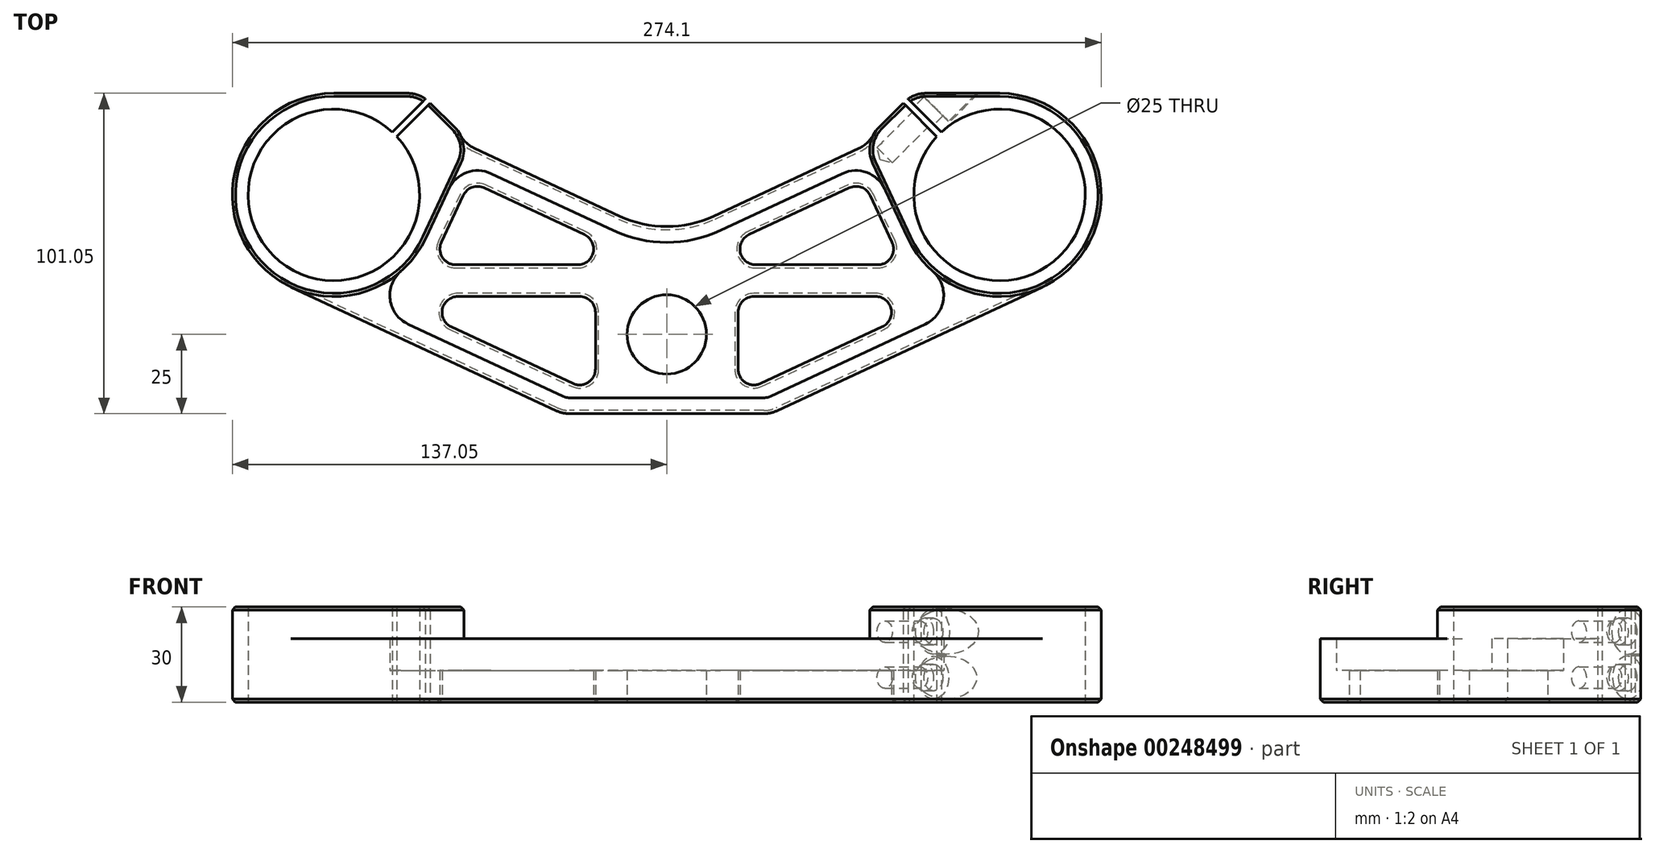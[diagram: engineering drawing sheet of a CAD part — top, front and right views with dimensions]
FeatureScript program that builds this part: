
annotation { "Feature Type Name" : "Feature", "Feature Type Description" : "" }
export const myFeature = defineFeature(function(context is Context, id is Id, definition is map)
    precondition{}
    {
        {
            var Q0;
            Q0=qCreatedBy(makeId("Top.planeOp"),FACE);
            var sketch = newSketch(context, id + "F0", { "sketchPlane" : qUnion([Q0])});
            skCircle(sketch, "E0", {"center": v(0, 0) * mm, "radius": 12.5 * mm});
            skArc(sketch, "E1", {"start": v(-86.6, 63.82) * mm, "mid": v(-124.13, 24.87) * mm, "end": v(-85.18, 62.4) * mm});
            skArc(sketch, "E2", {"start": v(85.18, 62.4) * mm, "mid": v(124.13, 24.87) * mm, "end": v(86.6, 63.82) * mm});
            skArc(sketch, "E3", {"start": v(75.95, 30.46) * mm, "mid": v(132.03, 26.78) * mm, "end": v(105, 76.05) * mm});
            skLineSegment(sketch, "E4", {"start": v(-30.65, -25) * mm, "end": v(30.65, -25) * mm});
            skLineSegment(sketch, "E5", {"start": v(-118.9, 15.12) * mm, "end": v(-34.88, -24.06) * mm});
            skLineSegment(sketch, "E6", {"start": v(118.54, 14.95) * mm, "end": v(34.88, -24.06) * mm});
            skLineSegment(sketch, "E7", {"start": v(-105, 76.05) * mm, "end": v(-81.8, 76.05) * mm});
            skLineSegment(sketch, "E8", {"start": v(-74.6, 73) * mm, "end": v(-66.94, 65.34) * mm});
            skLineSegment(sketch, "E9", {"start": v(74.6, 73) * mm, "end": v(66.94, 65.34) * mm});
            skLineSegment(sketch, "E10.trimOffspring", {"start": v(81.8, 76.05) * mm, "end": v(105, 76.05) * mm});
            skArc(sketch, "E11.filletArc", {"start": v(-76.13, 74.29) * mm, "mid": v(-78.83, 75.6) * mm, "end": v(-81.8, 76.05) * mm});
            skArc(sketch, "E12.filletArc", {"start": v(81.8, 76.05) * mm, "mid": v(78.83, 75.6) * mm, "end": v(76.13, 74.29) * mm});
            skPoint(sketch, "E13.visualSharp", {"position": v(-32.87, -25) * mm});
            skArc(sketch, "E13.filletArc", {"start": v(-34.88, -24.06) * mm, "mid": v(-32.81, -24.76) * mm, "end": v(-30.65, -25) * mm});
            skPoint(sketch, "E14.visualSharp", {"position": v(32.87, -25) * mm});
            skArc(sketch, "E14.filletArc", {"start": v(30.65, -25) * mm, "mid": v(32.81, -24.76) * mm, "end": v(34.88, -24.06) * mm});
            skLineSegment(sketch, "E15", {"start": v(-75.95, 30.46) * mm, "end": v(-64.95, 54.04) * mm});
            skLineSegment(sketch, "E16", {"start": v(75.95, 30.46) * mm, "end": v(64.95, 54.04) * mm});
            skArc(sketch, "E17", {"start": v(-65.2, 63) * mm, "mid": v(-65.99, 64.24) * mm, "end": v(-66.94, 65.34) * mm});
            skArc(sketch, "E18", {"start": v(66.94, 65.34) * mm, "mid": v(65.99, 64.24) * mm, "end": v(65.2, 63) * mm});
            skLineSegment(sketch, "E19", {"start": v(-85.18, 62.4) * mm, "end": v(-74.6, 73) * mm});
            skLineSegment(sketch, "E20", {"start": v(-86.6, 63.82) * mm, "end": v(-76.13, 74.29) * mm});
            skLineSegment(sketch, "E21", {"start": v(85.18, 62.4) * mm, "end": v(74.6, 73) * mm});
            skLineSegment(sketch, "E22", {"start": v(86.6, 63.82) * mm, "end": v(76.13, 74.29) * mm});
            skLineSegment(sketch, "E23", {"start": v(-68, 2.42) * mm, "end": v(-29.61, -15.48) * mm});
            skLineSegment(sketch, "E24", {"start": v(68, 2.42) * mm, "end": v(29.61, -15.48) * mm});
            skLineSegment(sketch, "E25", {"start": v(-65.89, 11.95) * mm, "end": v(-27.5, 11.95) * mm});
            skPoint(sketch, "E26.visualSharp", {"position": v(0, 31.47) * mm});
            skLineSegment(sketch, "E27", {"start": v(-66.55, 21.95) * mm, "end": v(-28.1, 21.95) * mm});
            skLineSegment(sketch, "E28", {"start": v(-55.46, 50.74) * mm, "end": v(-16.9, 32.77) * mm});
            skLineSegment(sketch, "E29", {"start": v(55.46, 50.74) * mm, "end": v(16.9, 32.77) * mm});
            skArc(sketch, "E30.filletArc", {"start": v(-16.9, 32.77) * mm, "mid": v(0, 29.02) * mm, "end": v(16.9, 32.77) * mm});
            skLineSegment(sketch, "E31", {"start": v(-57.57, 46.21) * mm, "end": v(-25.98, 31.48) * mm});
            skLineSegment(sketch, "E32", {"start": v(57.57, 46.21) * mm, "end": v(25.98, 31.48) * mm});
            skLineSegment(sketch, "E33.trimOffspring", {"start": v(-71.09, 29.06) * mm, "end": v(-64.22, 43.8) * mm});
            skLineSegment(sketch, "E34.trimOffspring", {"start": v(28.1, 21.95) * mm, "end": v(66.55, 21.95) * mm});
            skLineSegment(sketch, "E35.trimOffspring", {"start": v(71.09, 29.06) * mm, "end": v(64.22, 43.8) * mm});
            skPoint(sketch, "E36.orphan", {"position": v(105, 11.95) * mm});
            skPoint(sketch, "E37.orphan", {"position": v(88.44, 11.95) * mm});
            skLineSegment(sketch, "E38", {"start": v(-22.5, 6.95) * mm, "end": v(-22.5, -10.95) * mm});
            skLineSegment(sketch, "E39", {"start": v(22.5, 6.95) * mm, "end": v(22.5, -10.95) * mm});
            skLineSegment(sketch, "E40.trimOffspring", {"start": v(27.5, 11.95) * mm, "end": v(65.89, 11.95) * mm});
            skPoint(sketch, "E41.visualSharp", {"position": v(-5.54, 21.95) * mm});
            skArc(sketch, "E41.filletArc", {"start": v(-28.1, 21.95) * mm, "mid": v(-23.21, 25.87) * mm, "end": v(-25.98, 31.48) * mm});
            skPoint(sketch, "E42.visualSharp", {"position": v(-62.1, 48.33) * mm});
            skArc(sketch, "E42.filletArc", {"start": v(-57.57, 46.21) * mm, "mid": v(-61.4, 46.38) * mm, "end": v(-64.22, 43.8) * mm});
            skPoint(sketch, "E43.visualSharp", {"position": v(-74.4, 21.95) * mm});
            skArc(sketch, "E43.filletArc", {"start": v(-71.09, 29.06) * mm, "mid": v(-70.77, 24.26) * mm, "end": v(-66.55, 21.95) * mm});
            skArc(sketch, "E44.filletArc", {"start": v(-65.89, 11.95) * mm, "mid": v(-70.77, 8.03) * mm, "end": v(-68, 2.42) * mm});
            skPoint(sketch, "E45.visualSharp", {"position": v(-22.5, 11.95) * mm});
            skArc(sketch, "E45.filletArc", {"start": v(-22.5, 6.95) * mm, "mid": v(-23.96, 10.49) * mm, "end": v(-27.5, 11.95) * mm});
            skPoint(sketch, "E46.visualSharp", {"position": v(-22.5, -18.8) * mm});
            skArc(sketch, "E46.filletArc", {"start": v(-29.61, -15.48) * mm, "mid": v(-24.81, -15.17) * mm, "end": v(-22.5, -10.95) * mm});
            skPoint(sketch, "E47.visualSharp", {"position": v(22.5, 11.95) * mm});
            skArc(sketch, "E47.filletArc", {"start": v(27.5, 11.95) * mm, "mid": v(23.96, 10.49) * mm, "end": v(22.5, 6.95) * mm});
            skPoint(sketch, "E48.visualSharp", {"position": v(22.5, -18.8) * mm});
            skArc(sketch, "E48.filletArc", {"start": v(22.5, -10.95) * mm, "mid": v(24.81, -15.17) * mm, "end": v(29.61, -15.48) * mm});
            skArc(sketch, "E49.filletArc", {"start": v(68, 2.42) * mm, "mid": v(70.77, 8.03) * mm, "end": v(65.89, 11.95) * mm});
            skPoint(sketch, "E50.visualSharp", {"position": v(74.4, 21.95) * mm});
            skArc(sketch, "E50.filletArc", {"start": v(66.55, 21.95) * mm, "mid": v(70.77, 24.26) * mm, "end": v(71.09, 29.06) * mm});
            skPoint(sketch, "E51.visualSharp", {"position": v(62.1, 48.33) * mm});
            skArc(sketch, "E51.filletArc", {"start": v(64.22, 43.8) * mm, "mid": v(61.4, 46.38) * mm, "end": v(57.57, 46.21) * mm});
            skPoint(sketch, "E52.visualSharp", {"position": v(5.54, 21.95) * mm});
            skArc(sketch, "E52.filletArc", {"start": v(25.98, 31.48) * mm, "mid": v(23.21, 25.87) * mm, "end": v(28.1, 21.95) * mm});
            skLineSegment(sketch, "E53", {"start": v(81.6, 3.24) * mm, "end": v(32.76, -19.53) * mm});
            skLineSegment(sketch, "E54", {"start": v(-81.6, 3.24) * mm, "end": v(-32.76, -19.53) * mm});
            skLineSegment(sketch, "E55", {"start": v(14.8, 37.3) * mm, "end": v(60.62, 58.67) * mm});
            skArc(sketch, "E56.trimOffspring", {"start": v(-105, 76.05) * mm, "mid": v(-132.03, 26.78) * mm, "end": v(-75.95, 30.46) * mm});
            skLineSegment(sketch, "E57", {"start": v(-60.62, 58.67) * mm, "end": v(-14.8, 37.3) * mm});
            skArc(sketch, "E58.filletArc", {"start": v(-14.8, 37.3) * mm, "mid": v(0, 34.02) * mm, "end": v(14.8, 37.3) * mm});
            skLineSegment(sketch, "E59", {"start": v(30.65, -20) * mm, "end": v(-30.65, -20) * mm});
            skArc(sketch, "E60.filletArc", {"start": v(30.65, -20) * mm, "mid": v(31.73, -19.88) * mm, "end": v(32.76, -19.53) * mm});
            skArc(sketch, "E61.filletArc", {"start": v(-32.76, -19.53) * mm, "mid": v(-31.73, -19.88) * mm, "end": v(-30.65, -20) * mm});
            skArc(sketch, "E62", {"start": v(-83.94, 19.84) * mm, "mid": v(-87.27, 10.9) * mm, "end": v(-81.6, 3.24) * mm});
            skArc(sketch, "E63", {"start": v(83.94, 19.84) * mm, "mid": v(87.27, 10.9) * mm, "end": v(81.6, 3.24) * mm});
            skArc(sketch, "E64", {"start": v(-68.75, 45.9) * mm, "mid": v(-63.1, 51.08) * mm, "end": v(-55.46, 50.74) * mm});
            skArc(sketch, "E65", {"start": v(55.46, 50.74) * mm, "mid": v(63.1, 51.08) * mm, "end": v(68.75, 45.9) * mm});
            skArc(sketch, "E66.filletArc", {"start": v(-65.2, 63) * mm, "mid": v(-63.26, 60.46) * mm, "end": v(-60.62, 58.67) * mm});
            skArc(sketch, "E67.filletArc", {"start": v(60.62, 58.67) * mm, "mid": v(63.26, 60.46) * mm, "end": v(65.2, 63) * mm});
            skArc(sketch, "E68", {"start": v(65.2, 63) * mm, "mid": v(64.02, 58.55) * mm, "end": v(64.95, 54.04) * mm});
            skArc(sketch, "E69", {"start": v(-65.2, 63) * mm, "mid": v(-64.02, 58.55) * mm, "end": v(-64.95, 54.04) * mm});
            skSolve(sketch);
        }
        {
            var Q0;
            Q0=makeQuery(id+"F0.imprint","IMPRINT",FACE,{"disambiguationData":[TD([[makeQuery(id+"F0.imprint","IMPRINT",EDGE,{"derivedFrom":sQuery(id+"F0.wireOp",EDGE,"E2")}),-1.0]])]});
            var Q1;
            Q1=makeQuery(id+"F0.imprint","IMPRINT",FACE,{"disambiguationData":[TD([[makeQuery(id+"F0.imprint","IMPRINT",EDGE,{"derivedFrom":sQuery(id+"F0.wireOp",EDGE,"E1")}),-1.0]])]});
            extrude(context, id + "F1", {"entities" : qUnion([Q0, Q1]), "depth" : 30 * mm, "offsetDistance" : 25 * mm});
        }
        {
            var Q0;
            Q0=makeQuery(id+"F0.imprint","IMPRINT",FACE,{"disambiguationData":[TD([[makeQuery(id+"F0.imprint","IMPRINT",EDGE,{"derivedFrom":sQuery(id+"F0.wireOp",EDGE,"E0")}),-1.0]])]});
            extrude(context, id + "F2", {"entities" : qUnion([Q0]), "operationType" : NewBodyOperationType.ADD, "depth" : 10 * mm, "offsetDistance" : 25 * mm});
        }
        {
            var Q0;
            Q0=makeQuery(id+"F0.imprint","IMPRINT",FACE,{"disambiguationData":[TD([[makeQuery(id+"F0.imprint","IMPRINT",EDGE,{"derivedFrom":sQuery(id+"F0.wireOp",EDGE,"E28")}),1.0]])]});
            var Q1;
            Q1=makeQuery(id+"F0.imprint","IMPRINT",FACE,{"disambiguationData":[TD([[makeQuery(id+"F0.imprint","IMPRINT",EDGE,{"derivedFrom":sQuery(id+"F0.wireOp",EDGE,"E4")}),1.0]])]});
            extrude(context, id + "F3", {"entities" : qUnion([Q0, Q1]), "operationType" : NewBodyOperationType.ADD, "depth" : 20 * mm, "offsetDistance" : 25 * mm});
        }
        {
            var Q0;
            Q0=makeQuery(id+"F1.opExtrude","CAP_EDGE",EDGE,{"disambiguationData":[OSD([sQuery(id+"F0.wireOp",EDGE,"E5")])],"isStart":true});
            var Q1;
            {var subQ0=sQuery(id+"F0.wireOp",EDGE,"E56.trimOffspring");Q1=makeQuery(id+"F1.opExtrude","CAP_EDGE",EDGE,{"disambiguationData":[OSD([subQ0]),TDD([makeQuery(id+"F0.imprint","IMPRINT",EDGE,{"disambiguationData":[TD([[makeQuery(id+"F0.imprint","INTERSECT",VERTEX,{"derivedFrom":[sQuery(id+"F0.wireOp",EDGE,"E7"),subQ0]}),-1.0]])],"derivedFrom":subQ0})])],"isStart":true});}
            var Q2;
            Q2=makeQuery(id+"F1.opExtrude","CAP_EDGE",EDGE,{"disambiguationData":[OSD([sQuery(id+"F0.wireOp",EDGE,"E57")])],"isStart":true});
            var Q3;
            Q3=makeQuery(id+"F2.opExtrude","CAP_EDGE",EDGE,{"disambiguationData":[OSD([sQuery(id+"F0.wireOp",EDGE,"E24")])],"isStart":true});
            var Q4;
            Q4=makeQuery(id+"F2.opExtrude","CAP_EDGE",EDGE,{"disambiguationData":[OSD([sQuery(id+"F0.wireOp",EDGE,"E34.trimOffspring")])],"isStart":true});
            var Q5;
            Q5=makeQuery(id+"F2.opExtrude","CAP_EDGE",EDGE,{"disambiguationData":[OSD([sQuery(id+"F0.wireOp",EDGE,"E31")])],"isStart":true});
            var Q6;
            Q6=makeQuery(id+"F2.opExtrude","CAP_EDGE",EDGE,{"disambiguationData":[OSD([sQuery(id+"F0.wireOp",EDGE,"E25")])],"isStart":true});
            var Q7;
            {var subQ0=sQuery(id+"F0.wireOp",EDGE,"E3");Q7=makeQuery(id+"F1.opExtrude","CAP_EDGE",EDGE,{"disambiguationData":[OSD([subQ0]),TDD([makeQuery(id+"F0.imprint","IMPRINT",EDGE,{"disambiguationData":[TD([[makeQuery(id+"F0.imprint","INTERSECT",VERTEX,{"derivedFrom":[subQ0,sQuery(id+"F0.wireOp",EDGE,"E10.trimOffspring")]}),1.0]])],"derivedFrom":subQ0})])],"isStart":false});}
            var Q8;
            Q8=makeQuery(id+"F1.opExtrude","CAP_EDGE",EDGE,{"disambiguationData":[OSD([sQuery(id+"F0.wireOp",EDGE,"E58.filletArc")])],"isStart":false});
            var Q9;
            Q9=makeQuery(id+"F1.opExtrude","CAP_EDGE",EDGE,{"disambiguationData":[OSD([sQuery(id+"F0.wireOp",EDGE,"E8")])],"isStart":true});
            var Q10;
            Q10=makeQuery(id+"F1.opExtrude","CAP_EDGE",EDGE,{"disambiguationData":[OSD([sQuery(id+"F0.wireOp",EDGE,"E7")])],"isStart":false});
            chamfer(context, id + "F4", {"entities" : qUnion([Q0, Q1, Q2, Q3, Q4, Q5, Q6, Q7, Q8, Q9, Q10]), "width" : 1 * mm, "tangentPropagation" : true});
        }
        {
            var Q0;
            Q0=makeQuery(id+"F1.opExtrude","SWEPT_FACE",FACE,{"disambiguationData":[OSD([sQuery(id+"F0.wireOp",EDGE,"E21")])]});
            var sketch = newSketch(context, id + "F5", { "sketchPlane" : qUnion([Q0])});
            skCircle(sketch, "E70", {"center": v(-8.62, 7.75) * mm, "radius": 6.75 * mm});
            skCircle(sketch, "E71", {"center": v(-8.62, 22.25) * mm, "radius": 7.12 * mm});
            skCircle(sketch, "E72", {"center": v(-8.62, 22.25) * mm, "radius": 4.2 * mm});
            skCircle(sketch, "E73", {"center": v(-8.62, 7.75) * mm, "radius": 4.2 * mm});
            skSolve(sketch);
        }
        {
            var Q0;
            Q0=makeQuery(id+"F5.imprint","IMPRINT",FACE,{"disambiguationData":[TD([[makeQuery(id+"F5.imprint","IMPRINT",EDGE,{"derivedFrom":sQuery(id+"F5.wireOp",EDGE,"E70")}),1.0]])]});
            var Q1;
            Q1=makeQuery(id+"F5.imprint","IMPRINT",FACE,{"disambiguationData":[TD([[makeQuery(id+"F5.imprint","IMPRINT",EDGE,{"derivedFrom":sQuery(id+"F5.wireOp",EDGE,"E71")}),1.0]])]});
            var Q2;
            Q2=makeQuery(id+"F5.imprint","IMPRINT",FACE,{"disambiguationData":[TD([[makeQuery(id+"F5.imprint","IMPRINT",EDGE,{"derivedFrom":sQuery(id+"F5.wireOp",EDGE,"E72")}),1.0]])]});
            var Q3;
            Q3=makeQuery(id+"F5.imprint","IMPRINT",FACE,{"disambiguationData":[TD([[makeQuery(id+"F5.imprint","IMPRINT",EDGE,{"derivedFrom":sQuery(id+"F5.wireOp",EDGE,"E73")}),1.0]])]});
            var Q4;
            Q4=sQuery(id+"F5.wireOp",EDGE,"E70");
            var Q5;
            Q5=sQuery(id+"F5.wireOp",EDGE,"E71");
            extrude(context, id + "F6", {"entities" : qUnion([Q0, Q1, Q2, Q3]), "operationType" : NewBodyOperationType.REMOVE, "surfaceEntities" : qUnion([Q4, Q5]), "endBound" : BoundingType.UP_TO_NEXT, "depth" : 25 * mm, "hasOffset" : true, "offsetDistance" : 20 * mm, "offsetOppositeDirection" : true, "hasSecondDirection" : true, "secondDirectionOppositeDirection" : false, "secondDirectionDepth" : 6 * mm});
        }
        {
            var Q0;
            Q0=makeQuery(id+"F5.imprint","IMPRINT",FACE,{"disambiguationData":[TD([[makeQuery(id+"F5.imprint","IMPRINT",EDGE,{"derivedFrom":sQuery(id+"F5.wireOp",EDGE,"E73")}),1.0]])]});
            var Q1;
            Q1=makeQuery(id+"F5.imprint","IMPRINT",FACE,{"disambiguationData":[TD([[makeQuery(id+"F5.imprint","IMPRINT",EDGE,{"derivedFrom":sQuery(id+"F5.wireOp",EDGE,"E72")}),1.0]])]});
            extrude(context, id + "F7", {"entities" : qUnion([Q0, Q1]), "operationType" : NewBodyOperationType.REMOVE, "depth" : 25 * mm, "offsetDistance" : 25 * mm});
        }
        {
            var Q0;
            Q0=sQuery(id+"F5.wireOp",VERTEX,"E70.center");
            var Q1;
            Q1=sQuery(id+"F5.wireOp",VERTEX,"E71.center");
            var Q2;
            Q2=makeQuery(id+"F1.opExtrude","SWEPT_BODY",BODY,{"disambiguationData":[OSD([sQuery(id+"F0.wireOp",EDGE,"E1"),sQuery(id+"F0.wireOp",EDGE,"E7"),sQuery(id+"F0.wireOp",EDGE,"E8"),sQuery(id+"F0.wireOp",EDGE,"E11.filletArc"),sQuery(id+"F0.wireOp",EDGE,"E15"),sQuery(id+"F0.wireOp",EDGE,"E17"),sQuery(id+"F0.wireOp",EDGE,"E19"),sQuery(id+"F0.wireOp",EDGE,"E20"),sQuery(id+"F0.wireOp",EDGE,"E56.trimOffspring"),sQuery(id+"F0.wireOp",EDGE,"E69")])]});
            hole(context, id + "F8", {"style" : HoleStyle.SIMPLE, "endStyle" : HoleEndStyle.BLIND, "standardTappedOrClearance" : lookupTablePath({ "standard" : "ISO", "engagement" : "75%", "pitch" : "1.25 mm", "size" : "M8", "type" : "Tapped" }), "standardBlindInLast" : lookupTablePath({ "standard" : "ISO", "engagement" : "75%", "pitch" : "1.25 mm", "size" : "M8", "type" : "Tapped" }), "holeDiameter" : 6.8 * mm, "majorDiameter" : 8 * mm, "showTappedDepth" : true, "holeDepth" : 15.75 * mm, "isTappedThrough" : true, "tappedDepth" : 12 * mm, "tapClearance" : 3, "locations" : qUnion([Q0, Q1]), "scope" : qUnion([Q2])});
        }
    });
